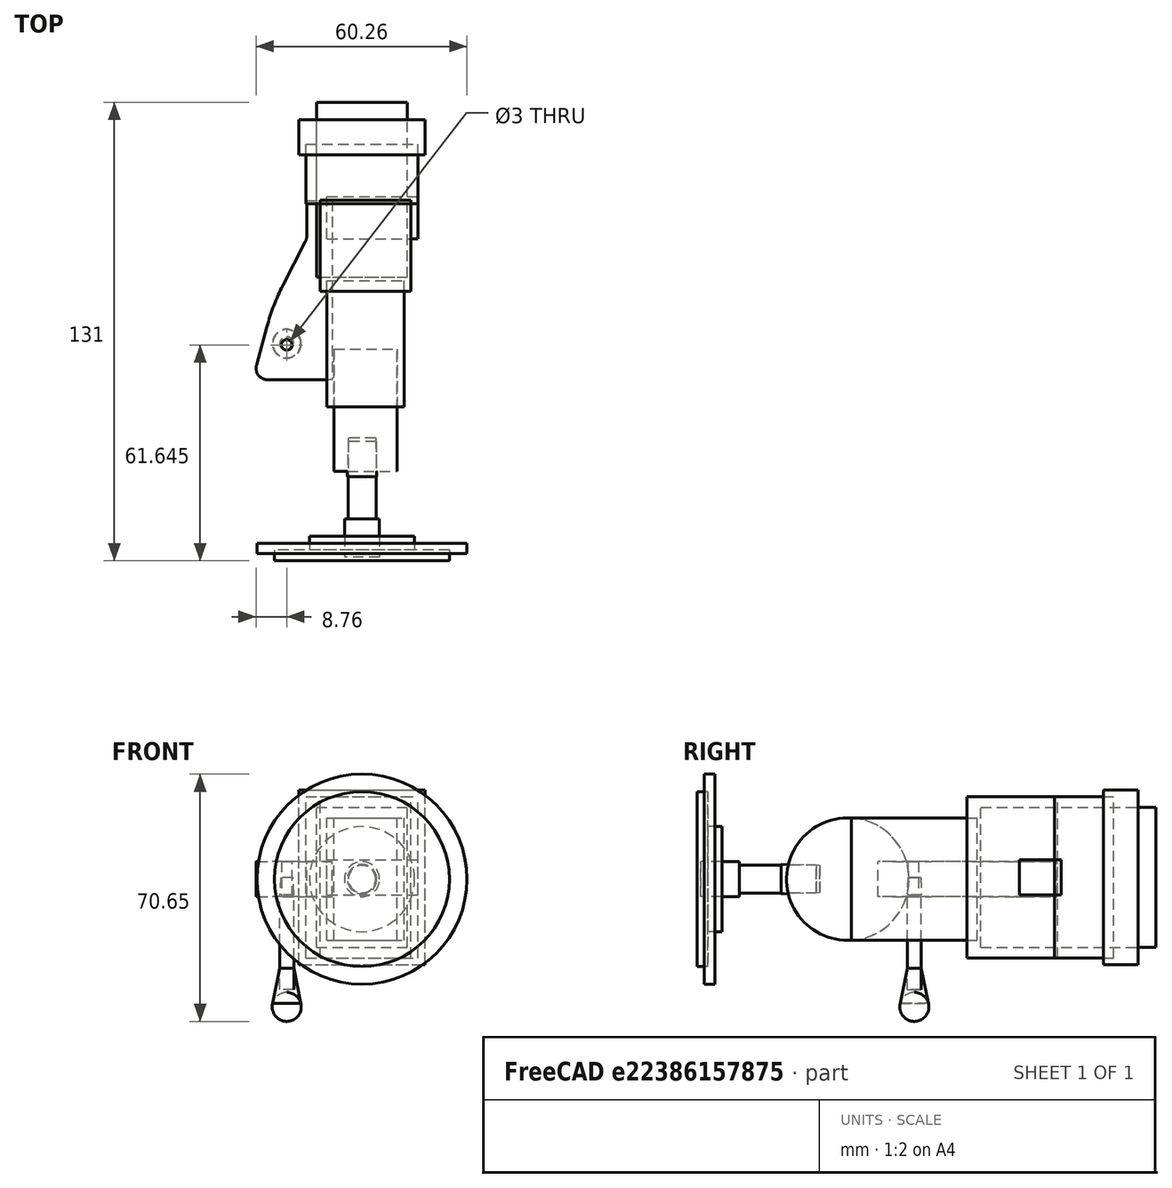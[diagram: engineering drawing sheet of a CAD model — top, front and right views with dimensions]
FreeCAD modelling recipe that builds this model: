
FCSTD DOCUMENT  (FreeCAD 0.16R6662 (Git))
Label: qtippholder-jw
License: All rights reserved
LicenseURL: http://en.wikipedia.org/wiki/All_rights_reserved
objects: Part::Cylinder×7, Part::Box×6, Part::Cone×3, Mesh::Feature×1, Sketcher::SketchObject×1, PartDesign::Pad×1, Part::Sphere×1
note: 20 computed .brp shape members not serialized (recipe doc carries the construction recipe); baked Part::Feature solids carry a one-line shape summary decoded from their .brp

FEATURE [Mesh::Feature] EarClnrHldr
  Placement = pos=(1.7939,1.69608,-3.31283) rot=(0,0,1;0rad)
FEATURE [Part::Box] Box  label="hut"
  Height = 50
  Length = 36
  Placement = pos=(14,116,11) rot=(0,0,1;0rad)
  Width = 10
FEATURE [Part::Box] Box001  label="stirn"
  Height = 46
  Length = 32
  Placement = pos=(16,102,13) rot=(0,0,1;0rad)
  Width = 17
FEATURE [Part::Box] Box002  label="gnack"
  Height = 10
  Length = 26
  Placement = pos=(22,92,31) rot=(0,0,1;0rad)
  Width = 12
FEATURE [Part::Box] Box003  label="augen"
  Height = 46
  Length = 26
  Placement = pos=(20,77,13) rot=(0,0,1;0rad)
  Width = 26
FEATURE [Part::Box] Box004  label="wangen"
  Height = 35
  Length = 22
  Placement = pos=(22,44,18) rot=(0,0,1;0rad)
  Width = 36
FEATURE [Part::Cylinder] Cylinder  label="kinn"
  Angle = 360
  Height = 18
  Placement = pos=(24,43,35.5) rot=(0,1,0;1.5708rad)
  Radius = 17.5
FEATURE [Sketcher::SketchObject] Sketch001
  Placement = pos=(22,44,36) rot=(0,0,1;0rad)
  sketch-geometry (10):
    g0: LineSegment StartX=1.5 StartY=7.67084 StartZ=0 EndX=-16.9205 EndY=7.67084 EndZ=0
    g1: LineSegment StartX=-20.1462 StartY=11.8885 StartZ=0 EndX=-17.1712 EndY=22.8519 EndZ=0
    g2: LineSegment StartX=-12.6256 StartY=34.6 StartZ=0 EndX=-6.24014 EndY=47.0658 EndZ=0
    g3: LineSegment StartX=-5.70418 StartY=49.2877 StartZ=0 EndX=-5.70418 EndY=58.874 EndZ=0
    g4: LineSegment StartX=-5.70418 StartY=58.874 StartZ=0 EndX=1.5 EndY=58.874 EndZ=0
    g5: LineSegment StartX=1.5 StartY=58.874 StartZ=0 EndX=1.5 EndY=7.67084 EndZ=0
    g6: ArcOfCircle CenterX=-16.9205 CenterY=11.0132 CenterZ=0 NormalX=0 NormalY=0 NormalZ=1 Radius=3.34236 StartAngle=2.87662 EndAngle=4.71239
    g7: ArcOfCircle CenterX=41.2664 CenterY=6.99453 CenterZ=0 NormalX=0 NormalY=0 NormalZ=1 Radius=60.5508 StartAngle=2.6682 EndAngle=2.87662
    g8: ArcOfCircle CenterX=-10.5778 CenterY=49.2877 CenterZ=0 NormalX=0 NormalY=0 NormalZ=1 Radius=4.87365 StartAngle=5.8098 EndAngle=6.28319
    g9: Circle CenterX=-11.5 CenterY=17.6445 CenterZ=0 NormalX=0 NormalY=0 NormalZ=1 Radius=1.5
  constraints (14):
    c: Horizontal(g0)
    c: Vertical(g3)
    c: Coincident(g3,g4)
    c: Horizontal(g4)
    c: Coincident(g4,g5)
    c: Coincident(g5,g0)
    c: Vertical(g5)
    c: Tangent(g0,g6) = 1.5708
    c: Tangent(g1,g6) = 1.5708
    c: Tangent(g1,g7) = 1.5708
    c: Tangent(g2,g7) = 1.5708
    c: Tangent(g2,g8) = -1.5708
    c: Tangent(g3,g8) = -1.5708
    c: Radius(g9) = 1.5
FEATURE [PartDesign::Pad] Pad  label="nase"
  Length = 4.5
  Length2 = 5.5
  Placement = pos=(22,44,36) rot=(0,0,1;0rad)
  Sketch = -> Sketch001
  Type = 4
FEATURE [Part::Cylinder] Cylinder002  label="bein"
  Angle = 360
  Height = 32
  Placement = pos=(32,34,35.5) rot=(1,0,0;1.5708rad)
  Radius = 4
FEATURE [Part::Cylinder] Cylinder003  label="bein001"
  Angle = 360
  Height = 11
  Placement = pos=(32,12,35.5) rot=(1,0,0;1.5708rad)
  Radius = 5
FEATURE [Part::Cylinder] Cylinder004  label="bein002"
  Angle = 360
  Height = 4
  Placement = pos=(32,7,35.5) rot=(1,0,0;1.5708rad)
  Radius = 15
FEATURE [Part::Cylinder] Cylinder005  label="bein003"
  Angle = 360
  Height = 3
  Placement = pos=(32,5,35.5) rot=(1,0,0;1.5708rad)
  Radius = 30
FEATURE [Part::Cylinder] Cylinder006  label="bein004"
  Angle = 360
  Height = 3
  Placement = pos=(32,3,35.5) rot=(1,0,0;1.5708rad)
  Radius = 25
FEATURE [Part::Box] Box005  label="kopfloch"
  Height = 40
  Length = 26
  Placement = pos=(19,81,16) rot=(0,0,1;0rad)
  Width = 50
FEATURE [Part::Cylinder] Cylinder007  label="staebchen"
  Angle = 360
  Height = 27
  Placement = pos=(10.5,62,4) rot=(0,0,1;0rad)
  Radius = 2
FEATURE [Part::Sphere] Sphere  label="Kugel"
  Angle1 = -90
  Angle2 = 90
  Angle3 = 360
  Placement = pos=(10.5,62,-1) rot=(0,0,1;0rad)
  Radius = 4.15
FEATURE [Part::Cone] Cone  label="Kegel"
  Angle = 360
  Height = 10
  Placement = pos=(10.5,62,0) rot=(0,0,1;0rad)
  Radius1 = 4
  Radius2 = 2
FEATURE [Part::Cone] Cone001  label="Kegel001"
  Angle = 360
  Height = 5
  Placement = pos=(10.5,62,31) rot=(0,0,1;0rad)
  Radius1 = 2
  Radius2 = 1.8
FEATURE [Part::Cone] Cone002  label="beinloch001"
  Angle = 360
  Height = 11
  Placement = pos=(32,35,35.5) rot=(1,0,0;1.5708rad)
  Radius1 = 3.9
  Radius2 = 4.2
